# Revit family: RUFO2 290xWSxH0150xx
name_source: partatom
category: Leuchten
units: mm (PartAtom-declared; Revit-internal decimal feet)

## family parameters
Basisbauteil = Fläche
Beim Laden mit Abzugskörper schneiden = Nein
Bemaßung runder Anschluss = Durchmesser verwenden
Gemeinsam genutzt = Nein
Lichtquelle = Ja
OmniClass-Nummer = 23.80.70.11
OmniClass-Titel = Luminaries for Internal Lighting
Raumberechnungspunkt = Nein
Teiletyp = Normal

## types (18) — shared parameters
Baugruppenkennzeichen = D5020200
Datei für fotometrisches Netz = RUFO2_290_H.IES
Emissionsform beim Rendern sichtbar = Nein
Farbfilter = 16777215
Farbtemperaturverschiebung bei Dämpfen der Lampe = <Keine Auswahl>
Hersteller = RIDI Leuchten GmbH
Lampe = LED
Neigungswinkel = 90.00°
URL = www.ridi.de
Von Kreisdurchmesser aussenden = 290 mm  [stored 0.951444 ft]
brand = RIDI
conformity mark = CE
electrical safety class = 1
height = 85 mm  [stored 0.278871 ft]
ingress protection (IP) code = IP40
length = 290 mm  [stored 0.951444 ft]
nominal frequency = 50-60Hz
nominal voltage = 230
voltage type (AC, DC, UC) = AC
width = 290 mm  [stored 0.951444 ft]
zero-valued in all types: Vorgabe-Ansicht

## per-type parameters (varying)
| type | Modell | Scheinlast | rated input power | weight |
| RUFO2 290NDWS840H0150 | 0420841 | 13 VA | 13 | 0.7 kg |
| RUFO2 290NDWS840H0150-RS | 0420841//396 | 13 VA | 13 | 0.75 kg |
| RUFO2 290NDWS830H0150 | 0420847 | 13 VA | 13 | 0.7 kg |
| RUFO2 290NDWS830H0150-RS | 0420847//396 | 13 VA | 13 | 0.75 kg |
| RUFO2 290NDWS840H0150-IK | 0420853 | 13 VA | 13 | 0.7 kg |
| RUFO2 290NDWS840H0150-IK-EDS3 | 0420853//377 | 13 VA | 13 | 0.95 kg |
| RUFO2 290NDWS840H0150-IK-RS | 0420853//396 | 13 VA | 13 | 0.75 kg |
| RUFO2 290NDWS830H0150-IK | 0420859 | 13 VA | 13 | 0.7 kg |
| RUFO2 290NDWS830H0150-IK-EDS3 | 0420859//377 | 13 VA | 13 | 0.95 kg |
| RUFO2 290NDWS830H0150-IK-RS | 0420859//396 | 13 VA | 13 | 0.75 kg |
| RUFO2 290DAWS840H0150 | 0430841 | 13 VA | 13 | 0.95 kg |
| RUFO2 290DAWS830H0150 | 0430847 | 13 VA | 13 | 0.7 kg |
| RUFO2 290DAWS840H0150-IK | 0430853 | 13 VA | 13 | 0.95 kg |
| RUFO2 290DAWS830H0150-IK | 0430859 | 13 VA | 13 | 0.7 kg |
| RUFO2 290NDWS840H0150-2K | 0420842 | 12 VA | 12 | 0.75 kg |
| RUFO2 290NDWS830H0150-2K | 0420848 | 12 VA | 12 | 0.75 kg |
| RUFO2 290NDWS840H0150-IK-2K | 0420854 | 12 VA | 12 | 0.75 kg |
| RUFO2 290NDWS830H0150-IK-2K | 0420860 | 12 VA | 12 | 0.75 kg |

note: column(s) folded — value = type name in every type: product name

note: [stored X ft] marks values corroborated as IEEE doubles in the binary element streams (Revit-internal decimal feet)
